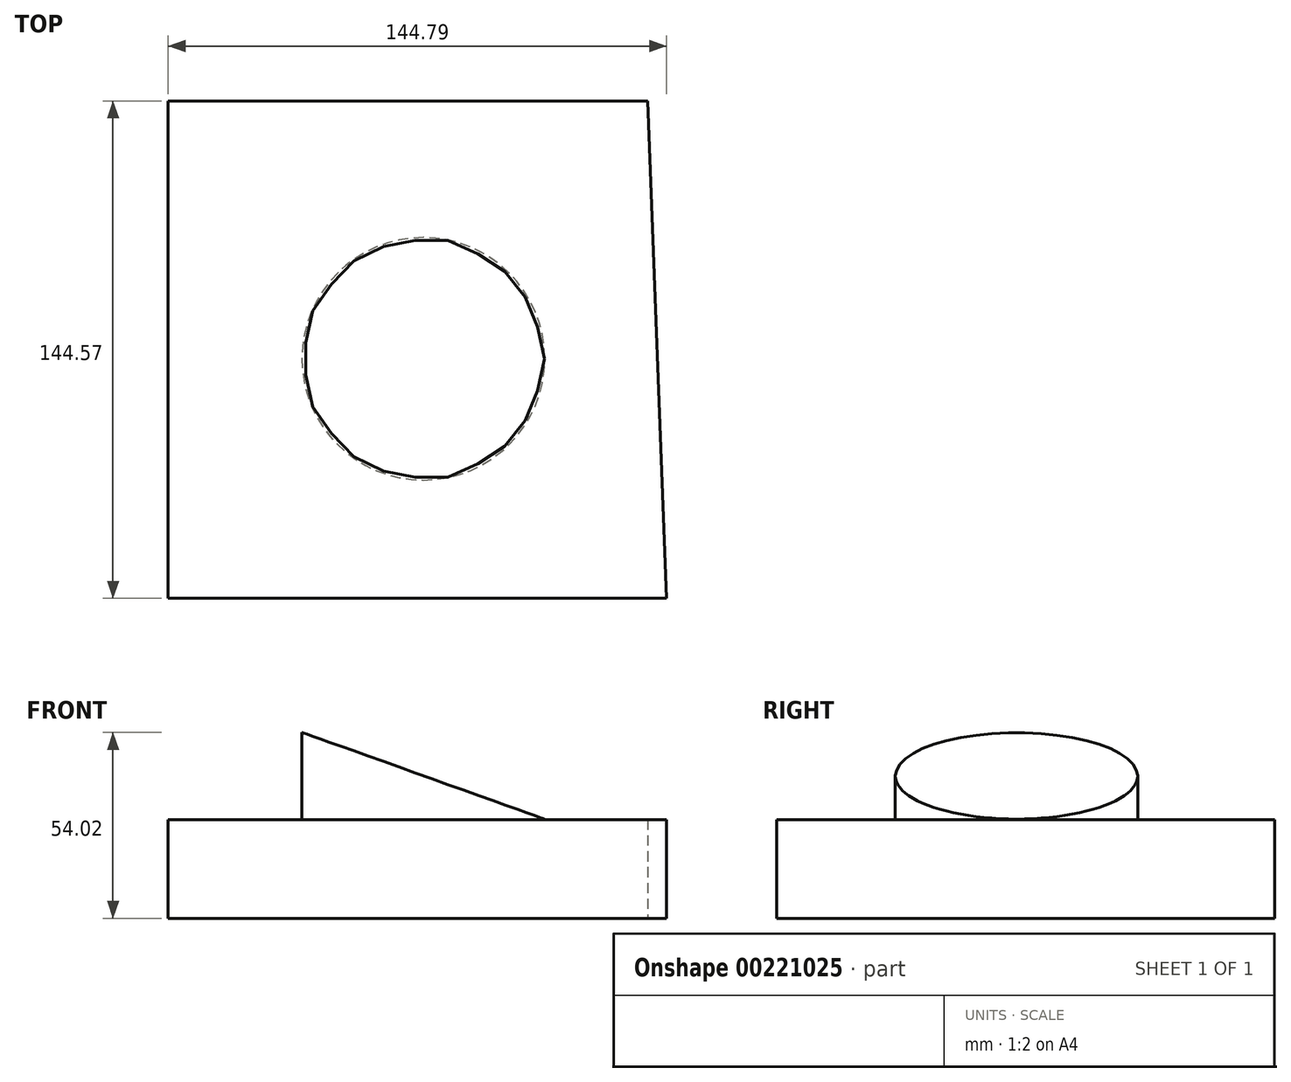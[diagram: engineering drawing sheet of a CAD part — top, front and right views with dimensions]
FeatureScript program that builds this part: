
annotation { "Feature Type Name" : "Feature", "Feature Type Description" : "" }
export const myFeature = defineFeature(function(context is Context, id is Id, definition is map)
    precondition{}
    {
        {
            var Q0;
            Q0=qCreatedBy(makeId("Top.planeOp"),FACE);
            var sketch = newSketch(context, id + "F0", { "sketchPlane" : qUnion([Q0])});
            skLineSegment(sketch, "E0", {"start": v(-74.12, 74.95) * mm, "end": v(-74.12, -69.62) * mm});
            skLineSegment(sketch, "E1", {"start": v(-74.12, -69.62) * mm, "end": v(70.67, -69.62) * mm});
            skLineSegment(sketch, "E2", {"start": v(-74.12, 74.95) * mm, "end": v(65.11, 74.95) * mm});
            skLineSegment(sketch, "E3", {"start": v(70.67, -69.62) * mm, "end": v(65.11, 74.95) * mm});
            skSolve(sketch);
        }
        {
            var Q0;
            Q0 = qSketchRegion(id + "F0", true);
            extrude(context, id + "F1", {"entities" : qUnion([Q0]), "depth" : 28.7 * mm});
        }
        {
            var Q0;
            Q0=makeQuery(id+"F1.opExtrude","CAP_FACE",FACE,{"disambiguationData":[OSD([sQuery(id+"F0.wireOp",EDGE,"E0"),sQuery(id+"F0.wireOp",EDGE,"E1"),sQuery(id+"F0.wireOp",EDGE,"E2"),sQuery(id+"F0.wireOp",EDGE,"E3")])],"isStart":false});
            var sketch = newSketch(context, id + "F2", { "sketchPlane" : qUnion([Q0])});
            skCircle(sketch, "E4", {"center": v(0, 0) * mm, "radius": 35.25 * mm});
            skSolve(sketch);
        }
        {
            var Q0;
            Q0=makeQuery(id+"F2.imprint","IMPRINT",FACE,{"disambiguationData":[TD([[makeQuery(id+"F2.imprint","IMPRINT",EDGE,{"derivedFrom":sQuery(id+"F2.wireOp",EDGE,"E4")}),1.0]])]});
            extrude(context, id + "F3", {"entities" : qUnion([Q0]), "operationType" : NewBodyOperationType.ADD, "depth" : 25.4 * mm});
        }
        {
            var Q0;
            Q0=makeQuery(id+"F1.opExtrude","SWEPT_FACE",FACE,{"disambiguationData":[OSD([sQuery(id+"F0.wireOp",EDGE,"E1")])]});
            var sketch = newSketch(context, id + "F4", { "sketchPlane" : qUnion([Q0])});
            skLineSegment(sketch, "E5", {"start": v(-38.84, 55.3) * mm, "end": v(35.62, 28.7) * mm});
            skLineSegment(sketch, "E6", {"start": v(35.62, 55) * mm, "end": v(35.62, 28.7) * mm});
            skLineSegment(sketch, "E7", {"start": v(-38.84, 55.3) * mm, "end": v(35.62, 55) * mm});
            skSolve(sketch);
        }
        {
            var Q0;
            Q0 = qSketchRegion(id + "F4", true);
            extrude(context, id + "F5", {"entities" : qUnion([Q0]), "operationType" : NewBodyOperationType.REMOVE, "endBound" : BoundingType.THROUGH_ALL, "oppositeDirection" : true, "depth" : 25.4 * mm});
        }
    });
